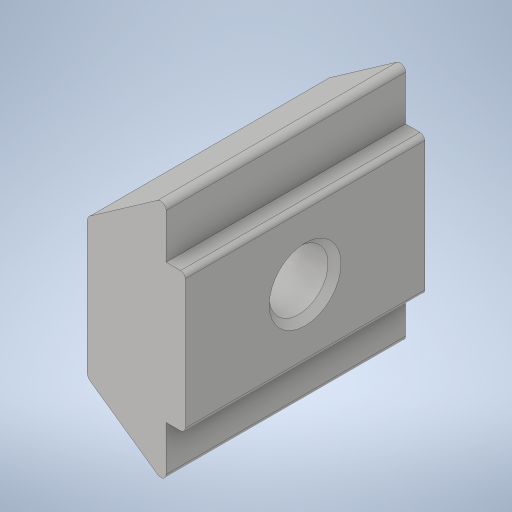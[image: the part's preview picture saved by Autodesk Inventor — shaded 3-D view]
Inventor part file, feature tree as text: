
AUTODESK INVENTOR PART (.ipt)
format: ipt  version: 2024 (Build 280153000, 153)  size: 262,144 bytes
history: native  units: mm
features: other x28, sketch x2, extrude x1, revolve x1
ambient origin geometry x8: Origin, YZ Plane, XZ Plane, XY Plane, X Axis, Y Axis, Z Axis, Center Point
bodies: Solid1 (feature_tree)
feature tree (32):
  extrude  "Extrusion1"  TaperAngle=360.0deg  [1 undecoded]
  revolve  "Revolution1"  [1 undecoded]
  other  "nut_XY"
  other  "nut_YZ"
  other  "nut_ZX"
  other  "nut_X"
  other  "nut_Y"
  other  "nut_Z"
  other  "nut_Center"
  other  "to_bolt_XY"
  other  "to_bolt_YZ"
  other  "to_bolt_ZX"
  other  "to_bolt_X"
  other  "to_bolt_Y"
  other  "to_bolt_Z"
  other  "to_bolt_Center"
  other  "to_frames_XY"
  other  "to_frames_YZ"
  other  "to_frames_ZX"
  other  "to_frames_X"
  other  "to_frames_Y"
  other  "to_frames_Z"
  other  "to_frames_Center"
  other  "to_lane_XY"
  other  "to_lane_YZ"
  other  "to_lane_ZX"
  other  "to_lane_X"
  other  "to_lane_Y"
  other  "to_lane_Z"
  other  "to_lane_Center"
  sketch  "Sketch_2"  dims[d0=10.0mm d1=0.0mm d2=360.0deg]
  sketch  "Sketch_5"  dims[d5=0.0mm d6=0.0mm]
note: 2 required parameter values undecoded (feature->parameter linkage not recoverable at this tier; creation-order binding heuristic only, values carry confidence <= 0.55)